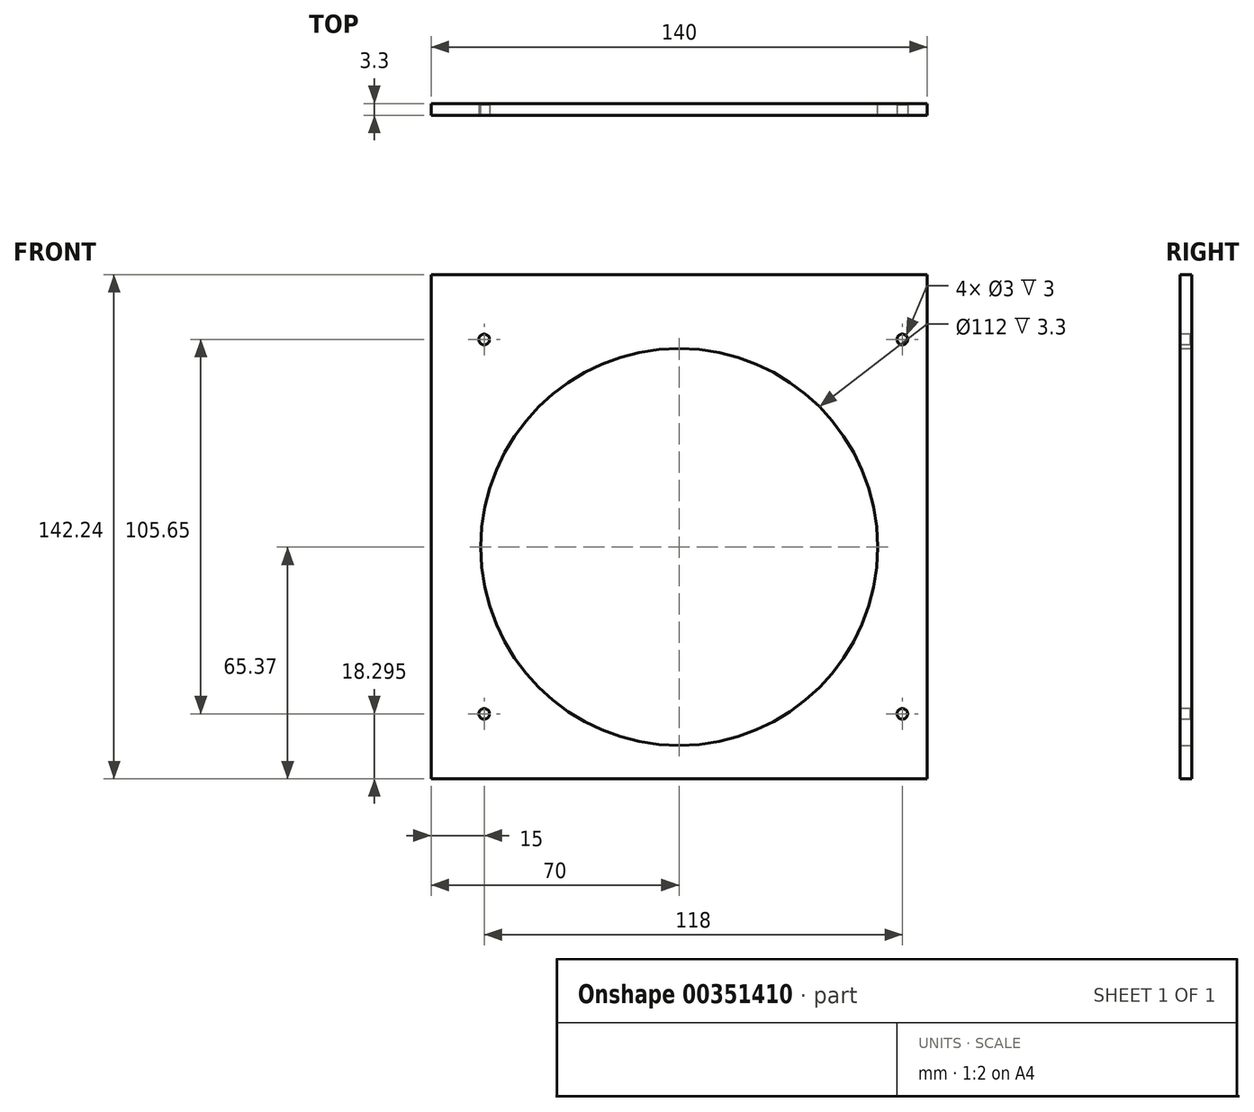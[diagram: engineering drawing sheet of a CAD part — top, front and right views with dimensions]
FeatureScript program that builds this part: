
annotation { "Feature Type Name" : "Feature", "Feature Type Description" : "" }
export const myFeature = defineFeature(function(context is Context, id is Id, definition is map)
    precondition{}
    {
        {
            var Q0;
            Q0=qCreatedBy(makeId("Front.planeOp"),FACE);
            var sketch = newSketch(context, id + "F0", { "sketchPlane" : qUnion([Q0])});
            skLineSegment(sketch, "E0.bottom", {"start": v(70, 71.12) * mm, "end": v(-70, 71.12) * mm});
            skLineSegment(sketch, "E0.top", {"start": v(70, -71.13) * mm, "end": v(-70, -71.13) * mm});
            skLineSegment(sketch, "E0.left", {"start": v(70, 71.13) * mm, "end": v(70, -71.13) * mm});
            skLineSegment(sketch, "E0.right", {"start": v(-70, 71.13) * mm, "end": v(-70, -71.13) * mm});
            skPoint(sketch, "E0.middle", {"position": v(0, 0) * mm});
            skCircle(sketch, "E1", {"center": v(0, -5.75) * mm, "radius": 56 * mm});
            skSolve(sketch);
        }
        {
            var Q0;
            Q0 = qSketchRegion(id + "F0", true);
            extrude(context, id + "F1", {"entities" : qUnion([Q0]), "depth" : 3.3 * mm});
        }
        {
            var Q0;
            Q0=makeQuery(id+"F1.opExtrude","CAP_FACE",FACE,{"disambiguationData":[OSD([sQuery(id+"F0.wireOp",EDGE,"E0.bottom"),sQuery(id+"F0.wireOp",EDGE,"E0.top"),sQuery(id+"F0.wireOp",EDGE,"E0.left"),sQuery(id+"F0.wireOp",EDGE,"E0.right"),sQuery(id+"F0.wireOp",EDGE,"E1")])],"isStart":false});
            var sketch = newSketch(context, id + "F2", { "sketchPlane" : qUnion([Q0])});
            skCircle(sketch, "E2", {"center": v(63, 52.82) * mm, "radius": 1.5 * mm});
            skCircle(sketch, "E3", {"center": v(-55, 52.82) * mm, "radius": 1.5 * mm});
            skCircle(sketch, "E4", {"center": v(-55, -52.83) * mm, "radius": 1.5 * mm});
            skCircle(sketch, "E5", {"center": v(63, -52.83) * mm, "radius": 1.5 * mm});
            skSolve(sketch);
        }
        {
            var Q0;
            Q0 = qSketchRegion(id + "F2", true);
            extrude(context, id + "F3", {"entities" : qUnion([Q0]), "operationType" : NewBodyOperationType.REMOVE, "oppositeDirection" : true, "depth" : 3 * mm});
        }
    });
